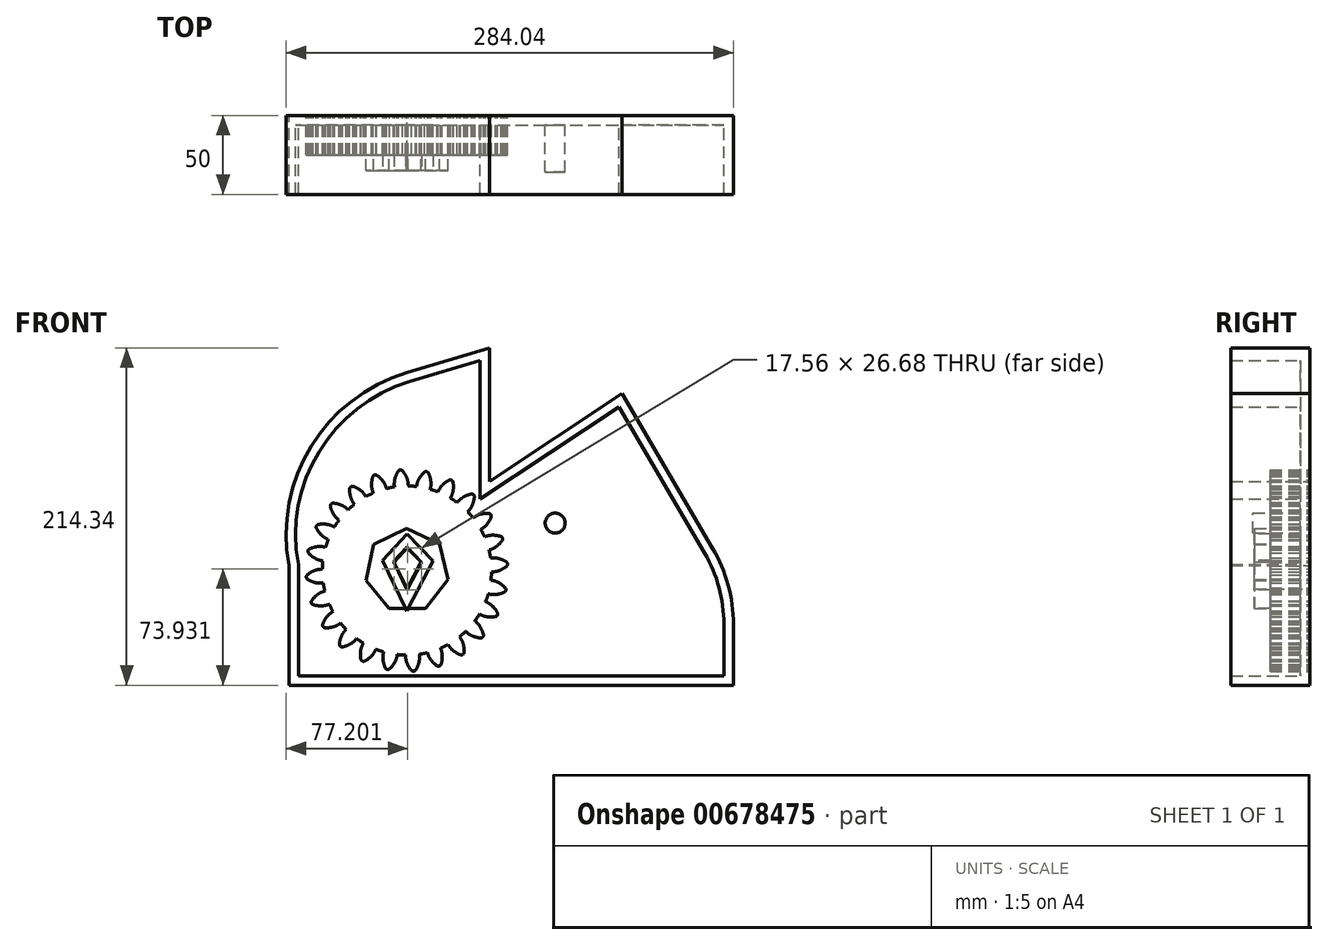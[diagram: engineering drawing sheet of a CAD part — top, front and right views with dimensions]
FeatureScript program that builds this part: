
annotation { "Feature Type Name" : "Feature", "Feature Type Description" : "" }
export const myFeature = defineFeature(function(context is Context, id is Id, definition is map)
    precondition{}
    {
        {
            var Q0;
            Q0=qCreatedBy(makeId("Front.planeOp"),FACE);
            var sketch = newSketch(context, id + "F0", { "sketchPlane" : qUnion([Q0])});
            skCircle(sketch, "E0", {"center": v(0, 0) * mm, "radius": 53.72 * mm});
            skCircle(sketch, "E1", {"center": v(0, 0) * mm, "radius": 58.67 * mm, "construction": true});
            skCircle(sketch, "E2", {"center": v(0, 0) * mm, "radius": 63.5 * mm, "construction": true});
            skLineSegment(sketch, "E3", {"start": v(0, 0) * mm, "end": v(0, 84.45) * mm, "construction": true});
            skLineSegment(sketch, "E4", {"start": v(0, 0) * mm, "end": v(-5.65, 86.22) * mm, "construction": true});
            skLineSegment(sketch, "E5", {"start": v(0, 58.67) * mm, "end": v(-58.15, 58.67) * mm, "construction": true});
            skLineSegment(sketch, "E6", {"start": v(0, 58.67) * mm, "end": v(-56.77, 38.01) * mm, "construction": true});
            skCircle(sketch, "E7", {"center": v(0, 0) * mm, "radius": 55.14 * mm, "construction": true});
            skCircle(sketch, "E8", {"center": v(0, 58.67) * mm, "radius": 14.6 * mm, "construction": true});
            skCircle(sketch, "E9", {"center": v(-13.72, 53.68) * mm, "radius": 14.6 * mm, "construction": true});
            skArc(sketch, "E10", {"start": v(0, 58.67) * mm, "mid": v(-1.23, 61.18) * mm, "end": v(-2.86, 63.44) * mm});
            skArc(sketch, "E11", {"start": v(0.88, 53.71) * mm, "mid": v(0.68, 56.24) * mm, "end": v(0, 58.67) * mm});
            skArc(sketch, "E12.MirrorCS", {"start": v(-7.66, 58.17) * mm, "mid": v(-6.77, 60.81) * mm, "end": v(-5.45, 63.27) * mm});
            skArc(sketch, "E13.MirrorCS", {"start": v(-7.88, 53.14) * mm, "mid": v(-8.02, 55.67) * mm, "end": v(-7.66, 58.17) * mm});
            skArc(sketch, "E14", {"start": v(-2.86, 63.44) * mm, "mid": v(-4.19, 63.93) * mm, "end": v(-5.45, 63.27) * mm});
            skCircle(sketch, "E15.cCircle", {"center": v(0, 0) * mm, "radius": 24.1 * mm, "construction": true});
            skLineSegment(sketch, "E15.0", {"start": v(-0.21, 26.75) * mm, "end": v(20.78, 16.84) * mm});
            skLineSegment(sketch, "E15.1", {"start": v(20.78, 16.84) * mm, "end": v(26.12, -5.75) * mm});
            skLineSegment(sketch, "E15.2", {"start": v(26.12, -5.75) * mm, "end": v(11.8, -24) * mm});
            skLineSegment(sketch, "E15.3", {"start": v(11.8, -24) * mm, "end": v(-11.42, -24.2) * mm});
            skLineSegment(sketch, "E15.4", {"start": v(-11.42, -24.2) * mm, "end": v(-26.03, -6.16) * mm});
            skLineSegment(sketch, "E15.5", {"start": v(-26.03, -6.16) * mm, "end": v(-21.04, 16.51) * mm});
            skLineSegment(sketch, "E15.6", {"start": v(-21.04, 16.51) * mm, "end": v(-0.21, 26.75) * mm});
            skPoint(sketch, "E15.0.midPoint", {"position": v(10.29, 21.8) * mm});
            skLineSegment(sketch, "E16", {"start": v(-8.48, 5.72) * mm, "end": v(0, 14.9) * mm});
            skLineSegment(sketch, "E17", {"start": v(-0.1, 14.9) * mm, "end": v(9.08, 5.53) * mm});
            skLineSegment(sketch, "E18", {"start": v(9.08, 5.53) * mm, "end": v(0, -11.84) * mm});
            skLineSegment(sketch, "E19", {"start": v(0, -11.84) * mm, "end": v(-8.48, 5.72) * mm});
            skSolve(sketch);
        }
        {
            var Q0;
            {var subQ0=sQuery(id+"F0.wireOp",EDGE,"E0");var subQ1=makeQuery(id+"F0.imprint","INTERSECT",VERTEX,{"derivedFrom":[subQ0,sQuery(id+"F0.wireOp",EDGE,"E11")]});Q0=makeQuery(id+"F0.imprint","IMPRINT",FACE,{"disambiguationData":[TD([[makeQuery(id+"F0.imprint","IMPRINT",EDGE,{"disambiguationData":[TD([[subQ1,-1.0]])],"derivedFrom":subQ0}),1.0]])]});}
            var Q1;
            Q1=makeQuery(id+"F0.imprint","IMPRINT",FACE,{"disambiguationData":[TD([[makeQuery(id+"F0.imprint","IMPRINT",EDGE,{"derivedFrom":sQuery(id+"F0.wireOp",EDGE,"E10")}),1.0]])]});
            var Q2;
            Q2=makeQuery(id+"F0.imprint","IMPRINT",FACE,{"disambiguationData":[TD([[makeQuery(id+"F0.imprint","IMPRINT",EDGE,{"derivedFrom":sQuery(id+"F0.wireOp",EDGE,"KPl7GWz1-QKYE-BqnT-suHZ-WVKqvGR7DCmq")}),1.0]])]});
            extrude(context, id + "F1", {"entities" : qUnion([Q0, Q1, Q2]), "depth" : 25 * mm, "offsetDistance" : 25 * mm});
        }
        {
            var Q0;
            Q0=makeQuery(id+"F1.opExtrude","SWEPT_BODY",BODY,{"disambiguationData":[OSD([sQuery(id+"F0.wireOp",EDGE,"E0"),sQuery(id+"F0.wireOp",EDGE,"E10"),sQuery(id+"F0.wireOp",EDGE,"E11"),sQuery(id+"F0.wireOp",EDGE,"E12.MirrorCS"),sQuery(id+"F0.wireOp",EDGE,"E13.MirrorCS"),sQuery(id+"F0.wireOp",EDGE,"E14")])]});
            var Q1;
            Q1=makeQuery(id+"F1.opExtrude","SWEPT_FACE",FACE,{"disambiguationData":[OSD([sQuery(id+"F0.wireOp",EDGE,"E0")])]});
            circularPattern(context, id + "F2", {"entities" : qUnion([Q0]), "axis" : qUnion([Q1]), "angle" : 360 * degree, "instanceCount" : 24, "equalSpace" : true});
        }
        {
            var Q0;
            Q0=makeQuery(id+"F0.imprint","IMPRINT",FACE,{"disambiguationData":[TD([[makeQuery(id+"F0.imprint","IMPRINT",EDGE,{"derivedFrom":sQuery(id+"F0.wireOp",EDGE,"E15.0")}),-1.0]])]});
            extrude(context, id + "F3", {"entities" : qUnion([Q0]), "operationType" : NewBodyOperationType.ADD, "depth" : 35 * mm, "offsetDistance" : 25 * mm});
        }
        {
            var Q0;
            Q0=qCreatedBy(makeId("Front.planeOp"),FACE);
            var sketch = newSketch(context, id + "F4", { "sketchPlane" : qUnion([Q0])});
            skLineSegment(sketch, "E20", {"start": v(-74.93, 3.2) * mm, "end": v(-74.93, -72.88) * mm});
            skLineSegment(sketch, "E21", {"start": v(-74.93, -72.88) * mm, "end": v(207.34, -72.88) * mm});
            skLineSegment(sketch, "E22", {"start": v(207.34, -72.88) * mm, "end": v(207.34, -34.16) * mm});
            skArc(sketch, "E23", {"start": v(0, 125.74) * mm, "mid": v(-60.9, 78.8) * mm, "end": v(-74.93, 3.2) * mm});
            skLineSegment(sketch, "E24", {"start": v(0, 125.74) * mm, "end": v(52.4, 141.46) * mm});
            skLineSegment(sketch, "E25", {"start": v(52.4, 141.46) * mm, "end": v(52.4, 56.55) * mm});
            skLineSegment(sketch, "E26", {"start": v(52.4, 56.55) * mm, "end": v(136.58, 112.52) * mm});
            skLineSegment(sketch, "E27", {"start": v(194.21, 14.19) * mm, "end": v(136.58, 112.52) * mm});
            skArc(sketch, "E28", {"start": v(207.34, -34.16) * mm, "mid": v(204, -9.11) * mm, "end": v(194.21, 14.19) * mm});
            skLineSegment(sketch, "E29", {"start": v(-8.28, 5.27) * mm, "end": v(0.2, 14.44) * mm});
            skLineSegment(sketch, "E30", {"start": v(0.11, 14.44) * mm, "end": v(9.28, 5.07) * mm});
            skLineSegment(sketch, "E31", {"start": v(9.28, 5.07) * mm, "end": v(0.2, -12.29) * mm});
            skLineSegment(sketch, "E32", {"start": v(0.2, -12.29) * mm, "end": v(-8.28, 5.27) * mm});
            skSolve(sketch);
        }
        {
            var Q0;
            Q0=makeQuery(id+"F4.imprint","IMPRINT",FACE,{"disambiguationData":[TD([[makeQuery(id+"F4.imprint","IMPRINT",EDGE,{"derivedFrom":sQuery(id+"F4.wireOp",EDGE,"E20")}),1.0]])]});
            extrude(context, id + "F5", {"entities" : qUnion([Q0]), "depth" : 50 * mm, "offsetDistance" : 25 * mm});
        }
        {
            var Q0;
            Q0=makeQuery(id+"F5.opExtrude","CAP_FACE",FACE,{"disambiguationData":[OSD([sQuery(id+"F4.wireOp",EDGE,"E20"),sQuery(id+"F4.wireOp",EDGE,"E21"),sQuery(id+"F4.wireOp",EDGE,"E22"),sQuery(id+"F4.wireOp",EDGE,"E23"),sQuery(id+"F4.wireOp",EDGE,"E24"),sQuery(id+"F4.wireOp",EDGE,"E25"),sQuery(id+"F4.wireOp",EDGE,"E26"),sQuery(id+"F4.wireOp",EDGE,"E27"),sQuery(id+"F4.wireOp",EDGE,"E28")])],"isStart":false});
            shell(context, id + "F6", {"entities" : qUnion([Q0]), "thickness" : 6 * mm});
        }
        {
            var Q0;
            {var subQ0=sQuery(id+"F4.wireOp",EDGE,"0ea7d122-6920-4461-aecb-10728f48c37e");var subQ1=sQuery(id+"F4.wireOp",EDGE,"E32");var subQ2=sQuery(id+"F4.wireOp",EDGE,"E31");var subQ3=sQuery(id+"F4.wireOp",EDGE,"E30");var subQ4=sQuery(id+"F4.wireOp",EDGE,"E29");var subQ5=sQuery(id+"F4.wireOp",EDGE,"E28");var subQ6=sQuery(id+"F4.wireOp",EDGE,"E27");var subQ7=sQuery(id+"F4.wireOp",EDGE,"E26");var subQ8=sQuery(id+"F4.wireOp",EDGE,"E25");var subQ9=sQuery(id+"F4.wireOp",EDGE,"E24");var subQ10=sQuery(id+"F4.wireOp",EDGE,"E23");var subQ11=sQuery(id+"F4.wireOp",EDGE,"E22");var subQ12=sQuery(id+"F4.wireOp",EDGE,"E21");var subQ13=sQuery(id+"F4.wireOp",EDGE,"E20");Q0=makeQuery(id+"F6.opShell","OFFSET_FACE",FACE,{"disambiguationData":[OSD([subQ13,subQ12,subQ11,subQ10,subQ9,subQ8,subQ7,subQ6,subQ5,subQ4,subQ3,subQ2,subQ1,subQ0]),TDD([makeQuery(id+"F5.opExtrude","CAP_FACE",FACE,{"disambiguationData":[OSD([subQ13,subQ12,subQ11,subQ10,subQ9,subQ8,subQ7,subQ6,subQ5,subQ4,subQ3,subQ2,subQ1,subQ0])],"isStart":false})]),OD(0.0)]});}
            extrude(context, id + "F7", {"entities" : qUnion([Q0]), "operationType" : NewBodyOperationType.REMOVE, "oppositeDirection" : true, "depth" : 25 * mm, "offsetDistance" : 25 * mm});
        }
        {
            var Q0;
            {var subQ0=sQuery(id+"F4.wireOp",EDGE,"E32");var subQ1=sQuery(id+"F4.wireOp",EDGE,"E31");var subQ2=sQuery(id+"F4.wireOp",EDGE,"E30");var subQ3=sQuery(id+"F4.wireOp",EDGE,"E29");var subQ4=sQuery(id+"F4.wireOp",EDGE,"E28");var subQ5=sQuery(id+"F4.wireOp",EDGE,"E27");var subQ6=sQuery(id+"F4.wireOp",EDGE,"E26");var subQ7=sQuery(id+"F4.wireOp",EDGE,"E25");var subQ8=sQuery(id+"F4.wireOp",EDGE,"E24");var subQ9=sQuery(id+"F4.wireOp",EDGE,"E23");var subQ10=sQuery(id+"F4.wireOp",EDGE,"E22");var subQ11=sQuery(id+"F4.wireOp",EDGE,"E21");var subQ12=sQuery(id+"F4.wireOp",EDGE,"E20");Q0=makeQuery(id+"F6.opShell","OFFSET_FACE",FACE,{"disambiguationData":[OSD([subQ12,subQ11,subQ10,subQ9,subQ8,subQ7,subQ6,subQ5,subQ4,subQ3,subQ2,subQ1,subQ0]),TDD([makeQuery(id+"F5.opExtrude","CAP_FACE",FACE,{"disambiguationData":[OSD([subQ12,subQ11,subQ10,subQ9,subQ8,subQ7,subQ6,subQ5,subQ4,subQ3,subQ2,subQ1,subQ0])],"isStart":true})])]});}
            var sketch = newSketch(context, id + "F8", { "sketchPlane" : qUnion([Q0])});
            skCircle(sketch, "E33", {"center": v(94.14, 30.12) * mm, "radius": 6.35 * mm});
            skSolve(sketch);
        }
        {
            var Q0;
            Q0=makeQuery(id+"F8.imprint","IMPRINT",FACE,{"disambiguationData":[TD([[makeQuery(id+"F8.imprint","IMPRINT",EDGE,{"derivedFrom":sQuery(id+"F8.wireOp",EDGE,"E33")}),1.0]])]});
            extrude(context, id + "F9", {"entities" : qUnion([Q0]), "operationType" : NewBodyOperationType.ADD, "depth" : 30 * mm, "offsetDistance" : 25 * mm});
        }
    });
